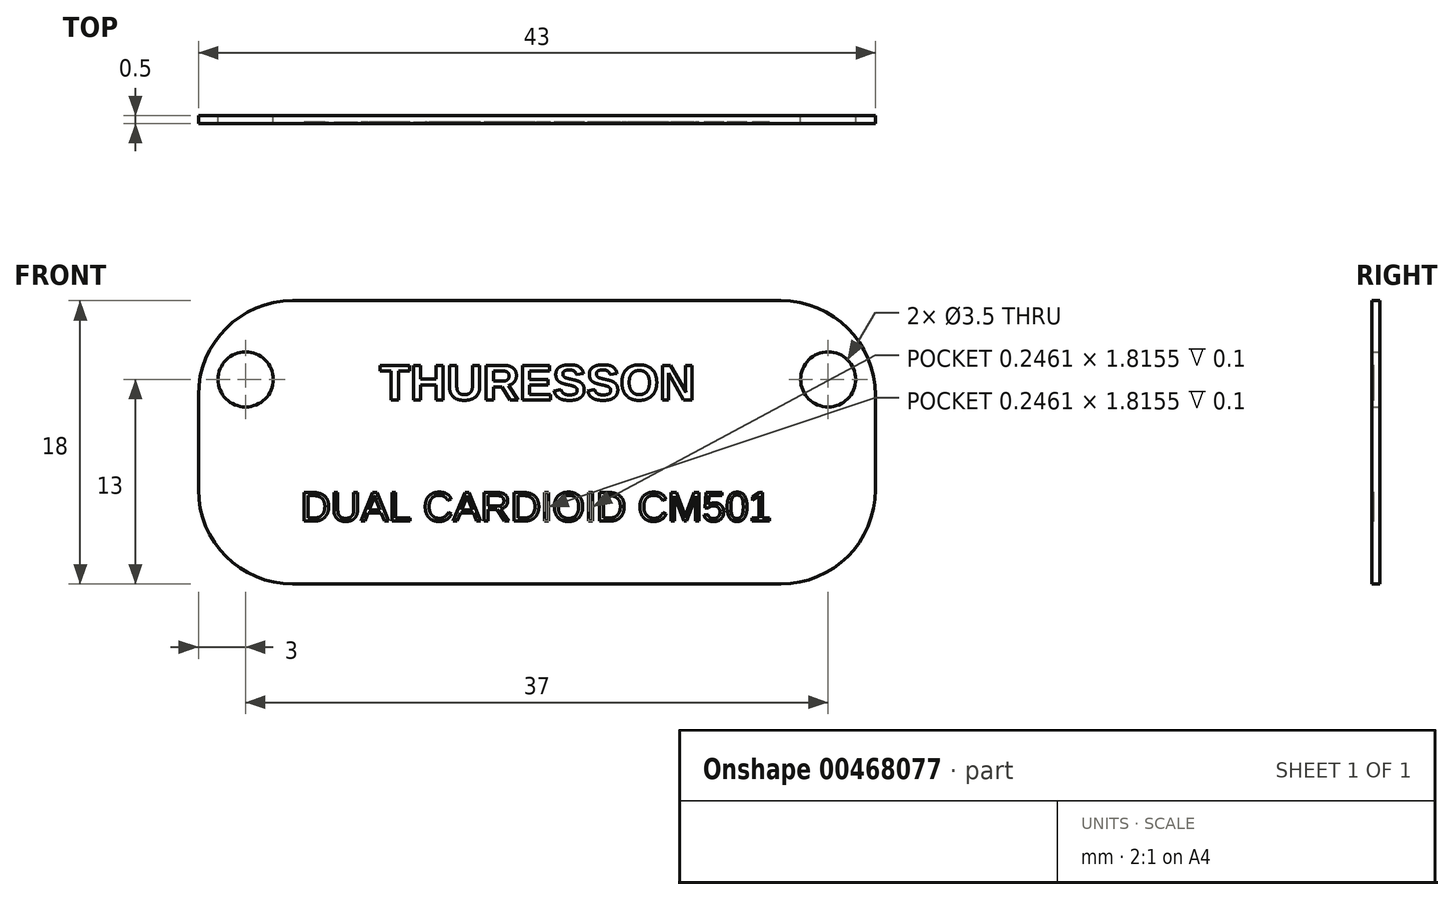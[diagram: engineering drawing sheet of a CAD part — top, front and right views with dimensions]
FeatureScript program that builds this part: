
annotation { "Feature Type Name" : "Feature", "Feature Type Description" : "" }
export const myFeature = defineFeature(function(context is Context, id is Id, definition is map)
    precondition{}
    {
        {
            var Q0;
            Q0=qCreatedBy(makeId("Front.planeOp"),FACE);
            var sketch = newSketch(context, id + "F0", { "sketchPlane" : qUnion([Q0])});
            skLineSegment(sketch, "E0.bottom", {"start": v(-15.5, 9) * mm, "end": v(15.5, 9) * mm});
            skLineSegment(sketch, "E0.top", {"start": v(-15.5, -9) * mm, "end": v(15.5, -9) * mm});
            skLineSegment(sketch, "E0.left", {"start": v(-21.5, 3) * mm, "end": v(-21.5, -3) * mm});
            skLineSegment(sketch, "E0.right", {"start": v(21.5, 3) * mm, "end": v(21.5, -3) * mm});
            skCircle(sketch, "E1", {"center": v(-18.5, 4) * mm, "radius": 1.75 * mm});
            skCircle(sketch, "E2", {"center": v(18.5, 4) * mm, "radius": 1.75 * mm});
            skPoint(sketch, "E3.visualSharp", {"position": v(-21.5, 9) * mm});
            skArc(sketch, "E3.filletArc", {"start": v(-15.5, 9) * mm, "mid": v(-19.74, 7.24) * mm, "end": v(-21.5, 3) * mm});
            skPoint(sketch, "E4.visualSharp", {"position": v(21.5, 9) * mm});
            skArc(sketch, "E4.filletArc", {"start": v(21.5, 3) * mm, "mid": v(19.74, 7.24) * mm, "end": v(15.5, 9) * mm});
            skPoint(sketch, "E5.visualSharp", {"position": v(21.5, -9) * mm});
            skArc(sketch, "E5.filletArc", {"start": v(15.5, -9) * mm, "mid": v(19.74, -7.24) * mm, "end": v(21.5, -3) * mm});
            skPoint(sketch, "E6.visualSharp", {"position": v(-21.5, -9) * mm});
            skArc(sketch, "E6.filletArc", {"start": v(-21.5, -3) * mm, "mid": v(-19.74, -7.24) * mm, "end": v(-15.5, -9) * mm});
            skLineSegment(sketch, "E7", {"start": v(0, 9) * mm, "end": v(0, -9) * mm, "construction": true});
            skLineSegment(sketch, "E8", {"start": v(-21.5, 0) * mm, "end": v(0, 0) * mm, "construction": true});
            skLineSegment(sketch, "E9", {"start": v(0, 0) * mm, "end": v(21.5, 0) * mm, "construction": true});
            skLineSegment(sketch, "E10", {"start": v(21.5, 0) * mm, "end": v(21.42, 0.54) * mm, "construction": true});
            skCircle(sketch, "E11", {"center": v(-18.5, 4) * mm, "radius": 6 * mm, "construction": true});
            skCircle(sketch, "E12", {"center": v(18.5, 4) * mm, "radius": 6 * mm, "construction": true});
            skSolve(sketch);
        }
        {
            var Q0;
            Q0 = qSketchRegion(id + "F0", true);
            var Q1;
            Q1 = qSketchRegion(id + "F2", true);
            extrude(context, id + "F1", {"entities" : qUnion([Q0, Q1]), "depth" : 0.5 * mm});
        }
        {
            var Q0;
            Q0=makeQuery(id+"F1.opExtrude","CAP_FACE",FACE,{"disambiguationData":[OSD([sQuery(id+"F0.wireOp",EDGE,"E0.bottom"),sQuery(id+"F0.wireOp",EDGE,"E0.top"),sQuery(id+"F0.wireOp",EDGE,"E0.left"),sQuery(id+"F0.wireOp",EDGE,"E0.right"),sQuery(id+"F0.wireOp",EDGE,"E1"),sQuery(id+"F0.wireOp",EDGE,"E2"),sQuery(id+"F0.wireOp",EDGE,"E3.filletArc"),sQuery(id+"F0.wireOp",EDGE,"E4.filletArc"),sQuery(id+"F0.wireOp",EDGE,"E5.filletArc"),sQuery(id+"F0.wireOp",EDGE,"E6.filletArc")])],"isStart":false});
            var sketch = newSketch(context, id + "F2", { "sketchPlane" : qUnion([Q0])});
            skText(sketch, "E13", { "text": "THURESSON", "fontName": "Arimo-Bold.ttf"});
            skText(sketch, "E14", { "text": "DUAL CARDIOID CM501", "fontName": "Arimo-Regular.ttf"});
            const initialGuessF2  = {"E13": [-0.01, 0.0027, 1, 0, 0.0023], "E14": [-0.015, -0.005, 1, 0, 0.0019]};
            skSetInitialGuess(sketch, initialGuessF2);
            skSolve(sketch);
        }
        {
            var Q0;
            Q0 = qSketchRegion(id + "F2", true);
            extrude(context, id + "F3", {"entities" : qUnion([Q0]), "operationType" : NewBodyOperationType.REMOVE, "oppositeDirection" : true, "depth" : 0.1 * mm});
        }
    });
